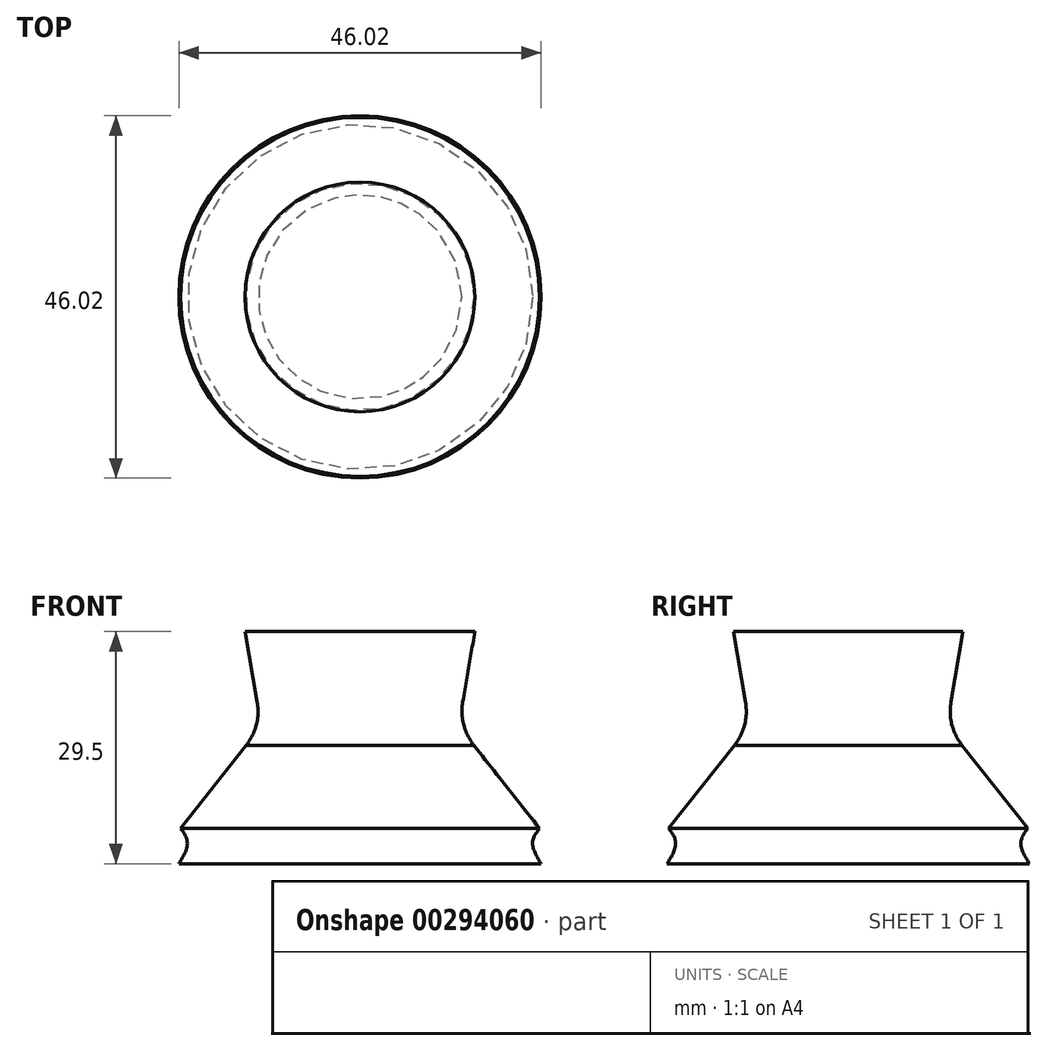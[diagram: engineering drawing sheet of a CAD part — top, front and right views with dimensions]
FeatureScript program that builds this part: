
annotation { "Feature Type Name" : "Feature", "Feature Type Description" : "" }
export const myFeature = defineFeature(function(context is Context, id is Id, definition is map)
    precondition{}
    {
        {
            var Q0;
            Q0=qCreatedBy(makeId("Top.planeOp"),FACE);
            var sketch = newSketch(context, id + "F0", { "sketchPlane" : qUnion([Q0])});
            skCircle(sketch, "E0", {"center": v(0, 0) * mm, "radius": 23.01 * mm});
            skSolve(sketch);
        }
        {
            var Q0;
            Q0=qCreatedBy(makeId("Top.planeOp"),FACE);
            cPlane(context, id + "F1", {"entities" : qUnion([Q0]), "cplaneType" : CPlaneType.OFFSET, "offset" : 3 * mm, "width" : 150 * mm, "height" : 150 * mm});
        }
        {
            var Q0;
            Q0=qCreatedBy(id+"F1.planeOp",FACE);
            var sketch = newSketch(context, id + "F2", { "sketchPlane" : qUnion([Q0])});
            skCircle(sketch, "E1", {"center": v(0, 0) * mm, "radius": 21.97 * mm});
            skSolve(sketch);
        }
        {
            var Q0;
            Q0=qCreatedBy(id+"F1.planeOp",FACE);
            cPlane(context, id + "F3", {"entities" : qUnion([Q0]), "cplaneType" : CPlaneType.OFFSET, "offset" : 1.5 * mm, "width" : 150 * mm, "height" : 150 * mm});
        }
        {
            var Q0;
            Q0=qCreatedBy(id+"F3.planeOp",FACE);
            var sketch = newSketch(context, id + "F4", { "sketchPlane" : qUnion([Q0])});
            skCircle(sketch, "E2", {"center": v(0, 0) * mm, "radius": 22.8 * mm});
            skSolve(sketch);
        }
        {
            var Q0;
            Q0 = qSketchRegion(id + "F0", true);
            var Q1;
            Q1 = qSketchRegion(id + "F2", true);
            var Q2;
            Q2 = qSketchRegion(id + "F4", true);
            loft(context, id + "F5", {"sheetProfilesArray" : [{ "sheetProfileEntities" : qUnion([Q0]) }, { "sheetProfileEntities" : qUnion([Q1]) }, { "sheetProfileEntities" : qUnion([Q2]) }]});
        }
        {
            var Q0;
            Q0=qCreatedBy(id+"F3.planeOp",FACE);
            cPlane(context, id + "F6", {"entities" : qUnion([Q0]), "cplaneType" : CPlaneType.OFFSET, "offset" : 25 * mm, "width" : 150 * mm, "height" : 150 * mm});
        }
        {
            var Q0;
            Q0=qCreatedBy(id+"F3.planeOp",FACE);
            cPlane(context, id + "F7", {"entities" : qUnion([Q0]), "cplaneType" : CPlaneType.OFFSET, "offset" : 13 * mm, "width" : 150 * mm, "height" : 150 * mm});
        }
        {
            var Q0;
            Q0=qCreatedBy(id+"F7.planeOp",FACE);
            var sketch = newSketch(context, id + "F8", { "sketchPlane" : qUnion([Q0])});
            skCircle(sketch, "E3", {"center": v(0, 0) * mm, "radius": 12.52 * mm});
            skSolve(sketch);
        }
        {
            var Q1;
            Q1=makeQuery(id+"F5.opLoft","CAP_FACE",FACE,{"disambiguationData":[OSD([makeQuery(id+"F4.imprint","IMPRINT",FACE,{"disambiguationData":[TD([[makeQuery(id+"F4.imprint","IMPRINT",EDGE,{"derivedFrom":sQuery(id+"F4.wireOp",EDGE,"E2")}),1.0]])]})])],"isStart":true});
            var Q2;
            Q2=makeQuery(id+"F8.imprint","IMPRINT",FACE,{"disambiguationData":[TD([[makeQuery(id+"F8.imprint","IMPRINT",EDGE,{"derivedFrom":sQuery(id+"F8.wireOp",EDGE,"E3")}),1.0]])]});
            loft(context, id + "F9", {"operationType" : NewBodyOperationType.ADD, "sheetProfilesArray" : [{ "sheetProfileEntities" : qUnion([Q1]) }, { "sheetProfileEntities" : qUnion([Q2]) }]});
        }
        {
            var Q0;
            Q0=qCreatedBy(id+"F6.planeOp",FACE);
            var sketch = newSketch(context, id + "F10", { "sketchPlane" : qUnion([Q0])});
            skCircle(sketch, "E4", {"center": v(0, 0) * mm, "radius": 14.6 * mm});
            skSolve(sketch);
        }
        {
            var Q1;
            Q1 = qSketchRegion(id + "F8", true);
            var Q2;
            Q2 = qSketchRegion(id + "F10", true);
            loft(context, id + "F11", {"operationType" : NewBodyOperationType.ADD, "sheetProfilesArray" : [{ "sheetProfileEntities" : qUnion([Q1]) }, { "sheetProfileEntities" : qUnion([Q2]) }]});
        }
        {
            var Q0;
            {var subQ0=sQuery(id+"F8.wireOp",EDGE,"E3");Q0=makeQuery(id+"F11.boolean.opBoolean","MERGE",EDGE,{"derivedFrom":[makeQuery(id+"F9.opLoft","MID_CAP_EDGE",EDGE,{"disambiguationData":[OSD([sQuery(id+"F0.wireOp",EDGE,"E0"),sQuery(id+"F4.wireOp",EDGE,"E2"),subQ0])],"capPos":1.0}),makeQuery(id+"F11.opLoft","MID_CAP_EDGE",EDGE,{"disambiguationData":[OSD([subQ0])],"capPos":0.0})]});}
            fillet(context, id + "F12", {"entities" : qUnion([Q0]), "radius" : 7 * mm, "tangentPropagation" : true, "allowEdgeOverflow" : false});
        }
    });
